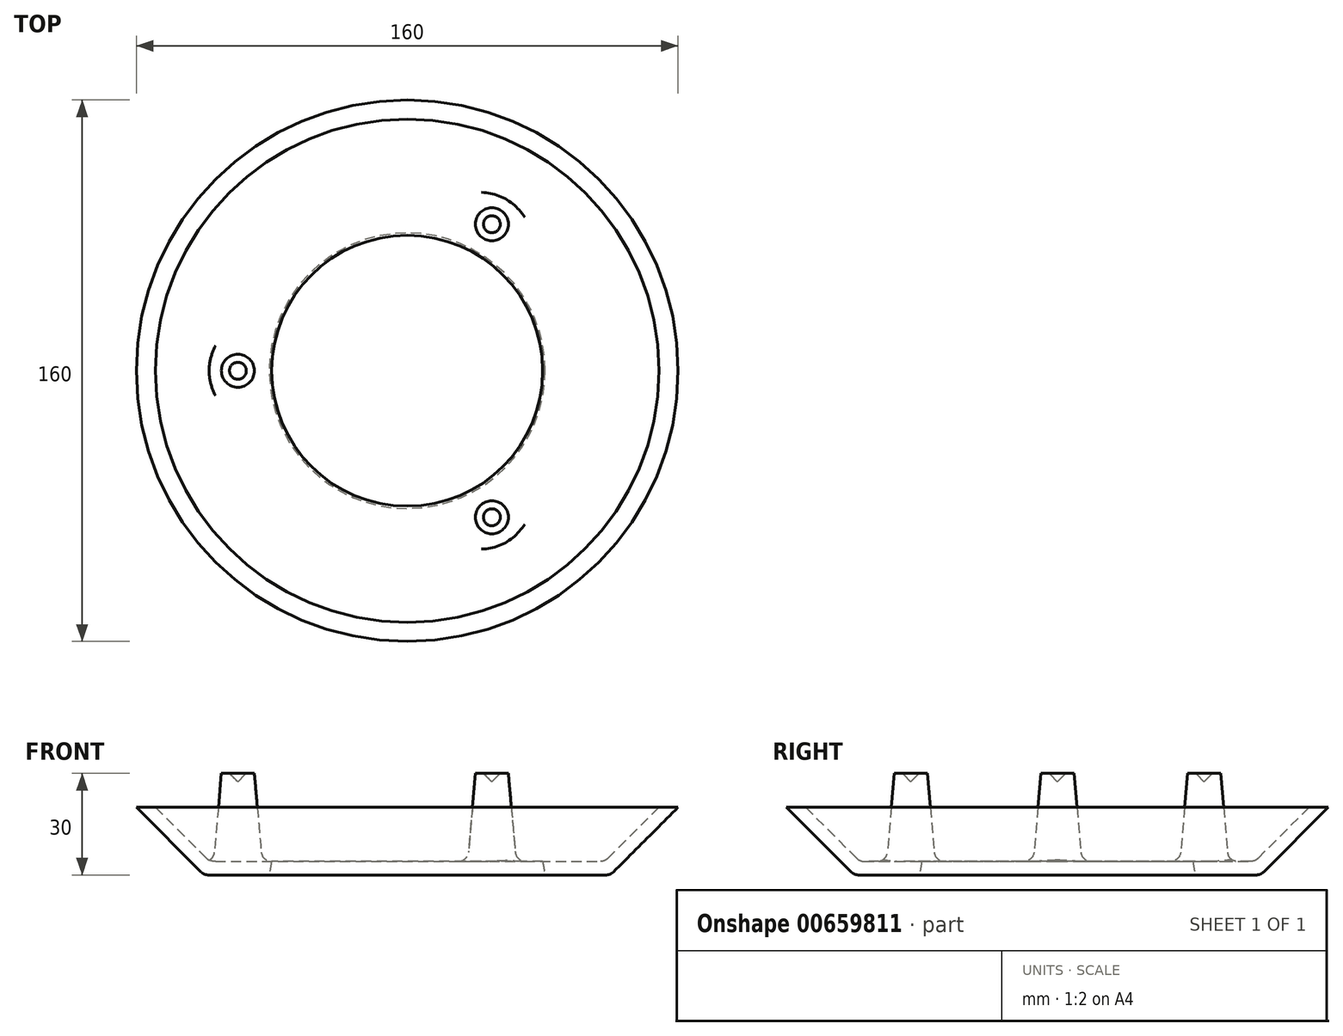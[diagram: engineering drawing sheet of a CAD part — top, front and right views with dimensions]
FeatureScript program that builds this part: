
annotation { "Feature Type Name" : "Feature", "Feature Type Description" : "" }
export const myFeature = defineFeature(function(context is Context, id is Id, definition is map)
    precondition{}
    {
        {
            var Q0;
            Q0=qCreatedBy(makeId("Front.planeOp"),FACE);
            var sketch = newSketch(context, id + "F0", { "sketchPlane" : qUnion([Q0])});
            skLineSegment(sketch, "E0", {"start": v(0, 0) * mm, "end": v(60, 0) * mm});
            skLineSegment(sketch, "E1", {"start": v(60, 0) * mm, "end": v(80, 20) * mm});
            skLineSegment(sketch, "E2", {"start": v(80, 20) * mm, "end": v(74.34, 20) * mm});
            skLineSegment(sketch, "E3", {"start": v(74.34, 20) * mm, "end": v(58.34, 4) * mm});
            skLineSegment(sketch, "E4", {"start": v(58.34, 4) * mm, "end": v(0, 4) * mm});
            skLineSegment(sketch, "E5", {"start": v(0, 4) * mm, "end": v(0, 0) * mm});
            skSolve(sketch);
        }
        {
            var Q0;
            Q0=qSketchRegion(id+"F0",true);
            var Q1;
            Q1=sQuery(id+"F0.wireOp",EDGE,"E5");
            revolve(context, id + "F1", {"entities" : qUnion([Q0]), "axis" : qUnion([Q1]), "revolveType" : RevolveType.FULL});
        }
        {
            var Q0;
            Q0=qCreatedBy(makeId("Top.planeOp"),FACE);
            var sketch = newSketch(context, id + "F2", { "sketchPlane" : qUnion([Q0])});
            skCircle(sketch, "E6", {"center": v(25, 43.3) * mm, "radius": 7.5 * mm});
            skCircle(sketch, "E7", {"center": v(-50, 0) * mm, "radius": 7.5 * mm});
            skLineSegment(sketch, "E8", {"start": v(0, 0) * mm, "end": v(31.77, 55.03) * mm, "construction": true});
            skLineSegment(sketch, "E9", {"start": v(0, 0) * mm, "end": v(26.35, -45.65) * mm, "construction": true});
            skCircle(sketch, "E10", {"center": v(25, -43.3) * mm, "radius": 7.5 * mm});
            skSolve(sketch);
        }
        {
            var Q0;
            Q0=qSketchRegion(id+"F2",true);
            var Q1;
            Q1=makeQuery(id+"F1.opRevolve","SWEPT_FACE",FACE,{"disambiguationData":[OSD([sQuery(id+"F0.wireOp",EDGE,"E2")])]});
            extrude(context, id + "F3", {"entities" : qUnion([Q0]), "operationType" : NewBodyOperationType.ADD, "depth" : 30 * mm, "endBoundEntityFace" : qUnion([Q1]), "offsetDistance" : 10 * mm, "hasDraft" : true, "draftAngle" : 5 * degree, "draftPullDirection" : true});
        }
        {
            var Q0;
            Q0=makeQuery(id+"F1.opRevolve","SWEPT_FACE",FACE,{"disambiguationData":[OSD([sQuery(id+"F0.wireOp",EDGE,"E4")])]});
            fillet(context, id + "F4", {"entities" : qUnion([Q0]), "radius" : 3 * mm, "tangentPropagation" : true, "allowEdgeOverflow" : false});
        }
        {
            var Q0;
            Q0=makeQuery(id+"F1.opRevolve","SWEPT_FACE",FACE,{"disambiguationData":[OSD([sQuery(id+"F0.wireOp",EDGE,"E0")])]});
            fillet(context, id + "F5", {"entities" : qUnion([Q0]), "radius" : 3 * mm, "tangentPropagation" : true, "allowEdgeOverflow" : false});
        }
        {
            var Q0;
            Q0=makeQuery(id+"F3.opExtrude","CAP_FACE",FACE,{"disambiguationData":[OSD([sQuery(id+"F2.wireOp",EDGE,"E7")])],"isStart":false});
            var sketch = newSketch(context, id + "F6", { "sketchPlane" : qUnion([Q0])});
            skCircle(sketch, "E11.0.0", {"center": v(-50, 0) * mm, "radius": 4.88 * mm, "construction": true});
            skCircle(sketch, "E12.0", {"center": v(25, 43.3) * mm, "radius": 4.88 * mm, "construction": true});
            skCircle(sketch, "E13.0", {"center": v(25, -43.3) * mm, "radius": 4.88 * mm, "construction": true});
            skCircle(sketch, "E14", {"center": v(25, 43.3) * mm, "radius": 2.5 * mm});
            skCircle(sketch, "E15", {"center": v(25, -43.3) * mm, "radius": 2.5 * mm});
            skCircle(sketch, "E16", {"center": v(-50, 0) * mm, "radius": 2.5 * mm});
            skSolve(sketch);
        }
        {
            var Q0;
            Q0=qSketchRegion(id+"F6",true);
            extrude(context, id + "F7", {"entities" : qUnion([Q0]), "operationType" : NewBodyOperationType.REMOVE, "oppositeDirection" : true, "depth" : 2.5 * mm, "offsetDistance" : 25 * mm, "hasDraft" : true, "draftAngle" : 45 * degree, "draftPullDirection" : true});
        }
        {
            var Q0;
            Q0=makeQuery(id+"F1.opRevolve","SWEPT_FACE",FACE,{"disambiguationData":[OSD([sQuery(id+"F0.wireOp",EDGE,"E4")])]});
            var sketch = newSketch(context, id + "F8", { "sketchPlane" : qUnion([Q0])});
            skCircle(sketch, "E17", {"center": v(0, 0) * mm, "radius": 40 * mm});
            skSolve(sketch);
        }
        {
            var Q0;
            Q0 = qSketchRegion(id + "F8", true);
            extrude(context, id + "F9", {"entities" : qUnion([Q0]), "operationType" : NewBodyOperationType.REMOVE, "endBound" : BoundingType.THROUGH_ALL, "oppositeDirection" : true, "depth" : 25 * mm, "offsetDistance" : 25 * mm, "hasDraft" : true, "draftAngle" : 10 * degree});
        }
    });
